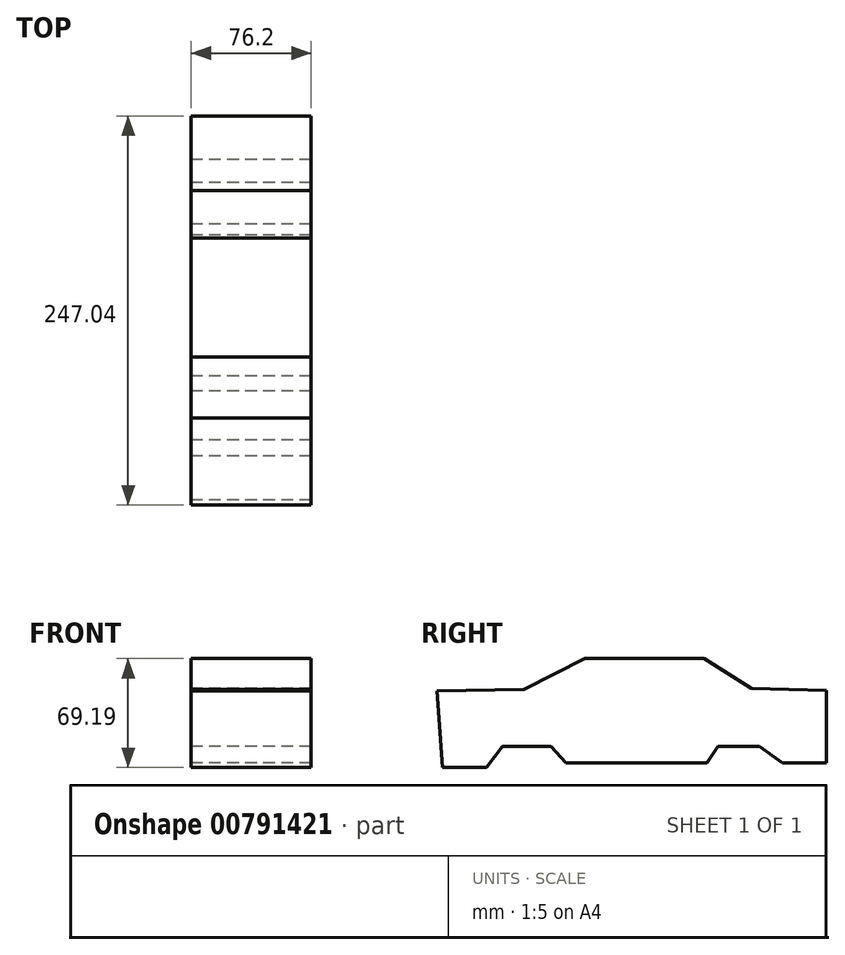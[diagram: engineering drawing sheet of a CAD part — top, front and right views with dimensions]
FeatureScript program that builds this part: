
annotation { "Feature Type Name" : "Feature", "Feature Type Description" : "" }
export const myFeature = defineFeature(function(context is Context, id is Id, definition is map)
    precondition{}
    {
        {
            var Q0;
            Q0=qCreatedBy(makeId("Right.planeOp"),FACE);
            var sketch = newSketch(context, id + "F0", { "sketchPlane" : qUnion([Q0])});
            skLineSegment(sketch, "E0", {"start": v(-90.68, -7.62) * mm, "end": v(-62.64, -7.62) * mm});
            skLineSegment(sketch, "E1", {"start": v(-62.64, -7.62) * mm, "end": v(-52.58, 5.8) * mm});
            skLineSegment(sketch, "E2", {"start": v(-52.58, 5.8) * mm, "end": v(-21.49, 5.8) * mm});
            skLineSegment(sketch, "E3", {"start": v(-21.49, 5.8) * mm, "end": v(-12.04, -4.88) * mm});
            skLineSegment(sketch, "E4", {"start": v(-12.04, -4.88) * mm, "end": v(77.57, -4.88) * mm});
            skLineSegment(sketch, "E5", {"start": v(77.57, -4.88) * mm, "end": v(84.58, 5.8) * mm});
            skLineSegment(sketch, "E6", {"start": v(84.58, 5.8) * mm, "end": v(110.8, 5.8) * mm});
            skLineSegment(sketch, "E7", {"start": v(110.8, 5.8) * mm, "end": v(125.43, -4.88) * mm});
            skLineSegment(sketch, "E8", {"start": v(125.43, -4.88) * mm, "end": v(153.16, -4.88) * mm});
            skLineSegment(sketch, "E9", {"start": v(153.16, -4.88) * mm, "end": v(153.16, 41.15) * mm});
            skLineSegment(sketch, "E10", {"start": v(153.16, 41.15) * mm, "end": v(68.88, 43.59) * mm});
            skLineSegment(sketch, "E11", {"start": v(68.88, 43.59) * mm, "end": v(32.61, 43.59) * mm});
            skLineSegment(sketch, "E12", {"start": v(32.61, 43.59) * mm, "end": v(-93.88, 40.84) * mm});
            skLineSegment(sketch, "E13", {"start": v(-93.88, 40.84) * mm, "end": v(-90.68, -7.62) * mm});
            skLineSegment(sketch, "E14", {"start": v(-38.66, 42.04) * mm, "end": v(0, 61.57) * mm});
            skLineSegment(sketch, "E15", {"start": v(0, 61.57) * mm, "end": v(75.6, 61.57) * mm});
            skLineSegment(sketch, "E16", {"start": v(75.6, 61.57) * mm, "end": v(105.7, 42.52) * mm});
            skSolve(sketch);
        }
        {
            var Q0;
            Q0=makeQuery(id+"F0.imprint","IMPRINT",FACE,{"disambiguationData":[TD([[makeQuery(id+"F0.imprint","IMPRINT",EDGE,{"derivedFrom":sQuery(id+"F0.wireOp",EDGE,"E0")}),1.0]])]});
            var Q1;
            {var subQ1=sQuery(id+"F0.wireOp",EDGE,"E11");Q1=makeQuery(id+"F0.imprint","IMPRINT",FACE,{"disambiguationData":[TD([[makeQuery(id+"F0.imprint","IMPRINT",EDGE,{"derivedFrom":subQ1}),-1.0]])]});}
            extrude(context, id + "F1", {"entities" : qUnion([Q0, Q1]), "depth" : 76.2 * mm, "offsetDistance" : 25.4 * mm});
        }
    });
